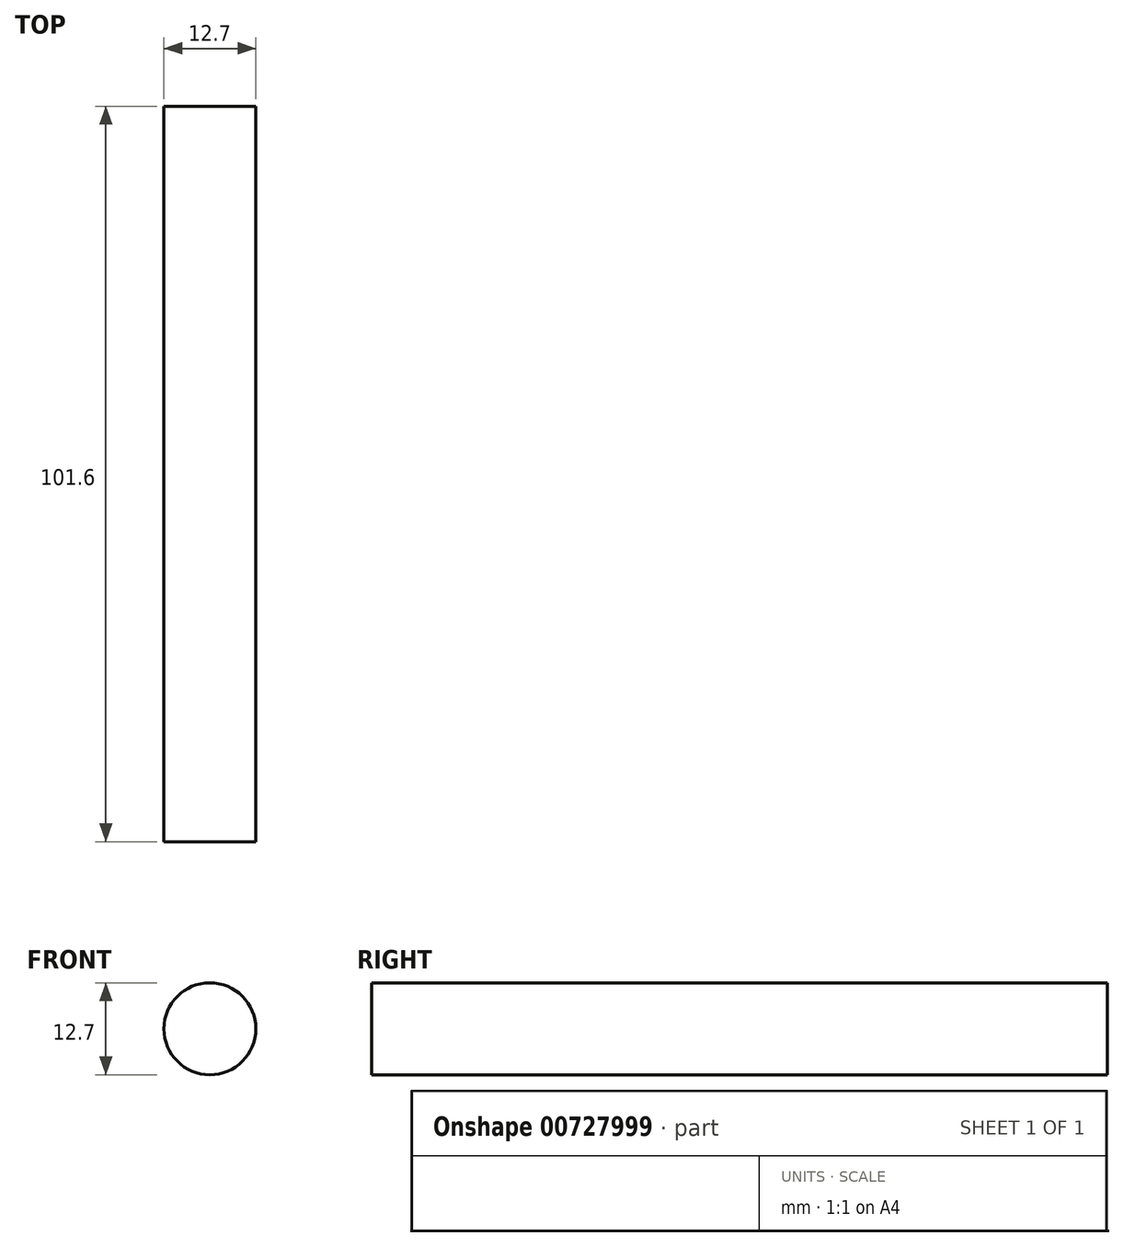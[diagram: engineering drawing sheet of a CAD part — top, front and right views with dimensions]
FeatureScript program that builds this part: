
annotation { "Feature Type Name" : "Feature", "Feature Type Description" : "" }
export const myFeature = defineFeature(function(context is Context, id is Id, definition is map)
    precondition{}
    {
        {
            var Q0;
            Q0=qCreatedBy(makeId("Front.planeOp"),FACE);
            var sketch = newSketch(context, id + "F0", { "sketchPlane" : qUnion([Q0])});
            skCircle(sketch, "E0", {"center": v(0, 0.75) * mm, "radius": 6.35 * mm});
            skSolve(sketch);
        }
        {
            var Q0;
            Q0=makeQuery(id+"F0.imprint","IMPRINT",FACE,{"disambiguationData":[TD([[makeQuery(id+"F0.imprint","IMPRINT",EDGE,{"derivedFrom":sQuery(id+"F0.wireOp",EDGE,"E0")}),1.0]])]});
            extrude(context, id + "F1", {"entities" : qUnion([Q0]), "depth" : 101.6 * mm, "offsetDistance" : 25.4 * mm});
        }
    });
